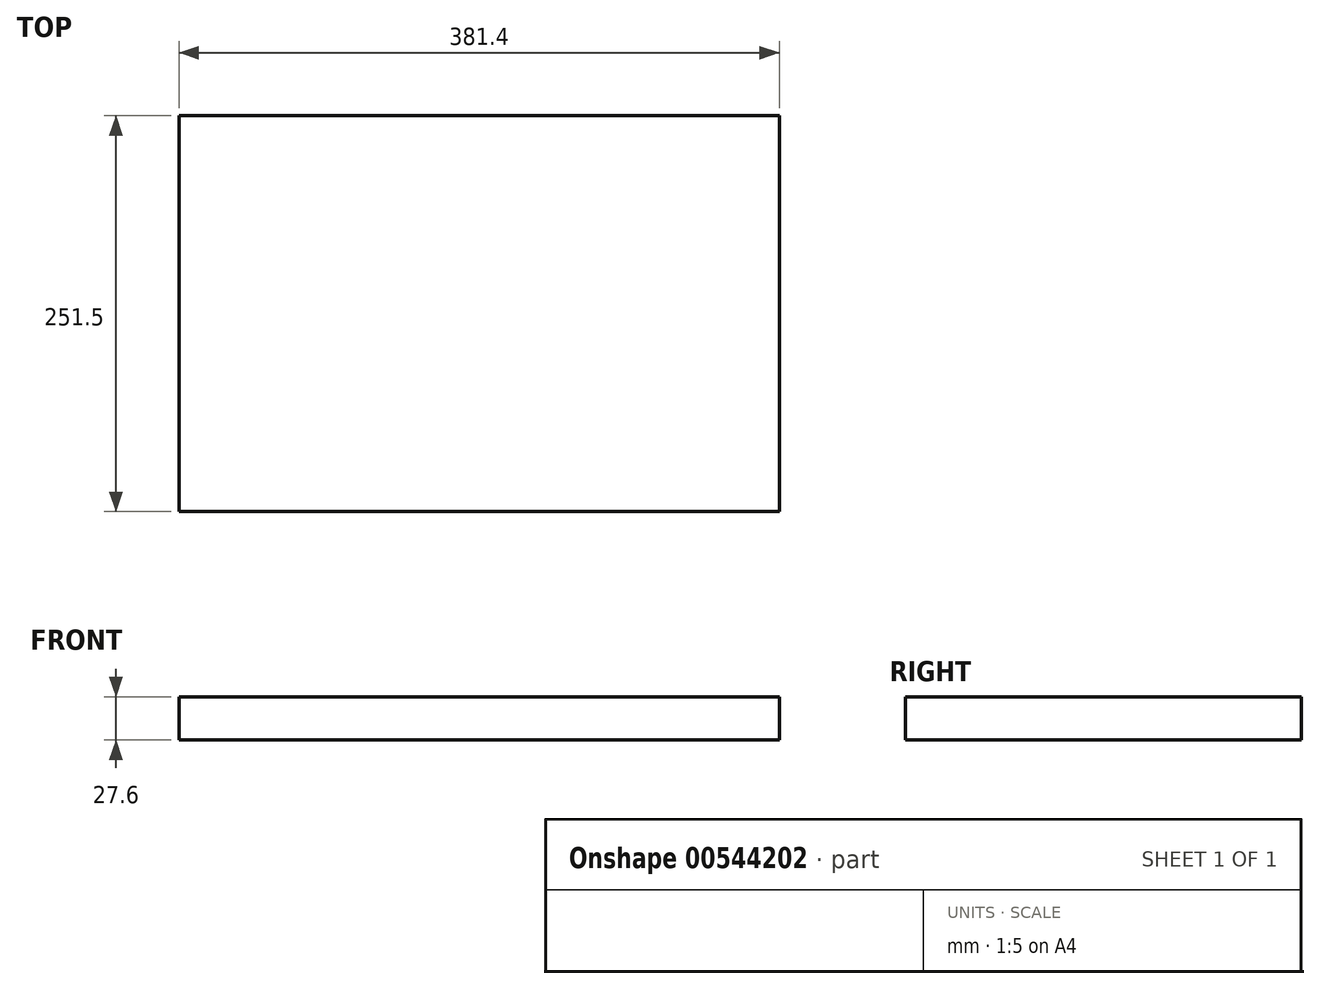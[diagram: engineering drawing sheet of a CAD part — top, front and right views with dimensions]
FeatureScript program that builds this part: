
annotation { "Feature Type Name" : "Feature", "Feature Type Description" : "" }
export const myFeature = defineFeature(function(context is Context, id is Id, definition is map)
    precondition{}
    {
        {
            var Q0;
            Q0=qCreatedBy(makeId("Top.planeOp"),FACE);
            var sketch = newSketch(context, id + "F0", { "sketchPlane" : qUnion([Q0])});
            skLineSegment(sketch, "E0.bottom", {"start": v(-232.35, 150.28) * mm, "end": v(149.05, 150.28) * mm});
            skLineSegment(sketch, "E0.top", {"start": v(-232.35, -101.22) * mm, "end": v(149.05, -101.22) * mm});
            skLineSegment(sketch, "E0.left", {"start": v(-232.35, 150.28) * mm, "end": v(-232.35, -101.22) * mm});
            skLineSegment(sketch, "E0.right", {"start": v(149.05, 150.28) * mm, "end": v(149.05, -101.22) * mm});
            skSolve(sketch);
        }
        {
            var Q0;
            Q0=makeQuery(id+"F0.imprint","IMPRINT",FACE,{"disambiguationData":[TD([[makeQuery(id+"F0.imprint","IMPRINT",EDGE,{"derivedFrom":sQuery(id+"F0.wireOp",EDGE,"E0.bottom")}),-1.0]])]});
            extrude(context, id + "F1", {"entities" : qUnion([Q0]), "depth" : 27.6 * mm, "offsetDistance" : 25 * mm});
        }
    });
